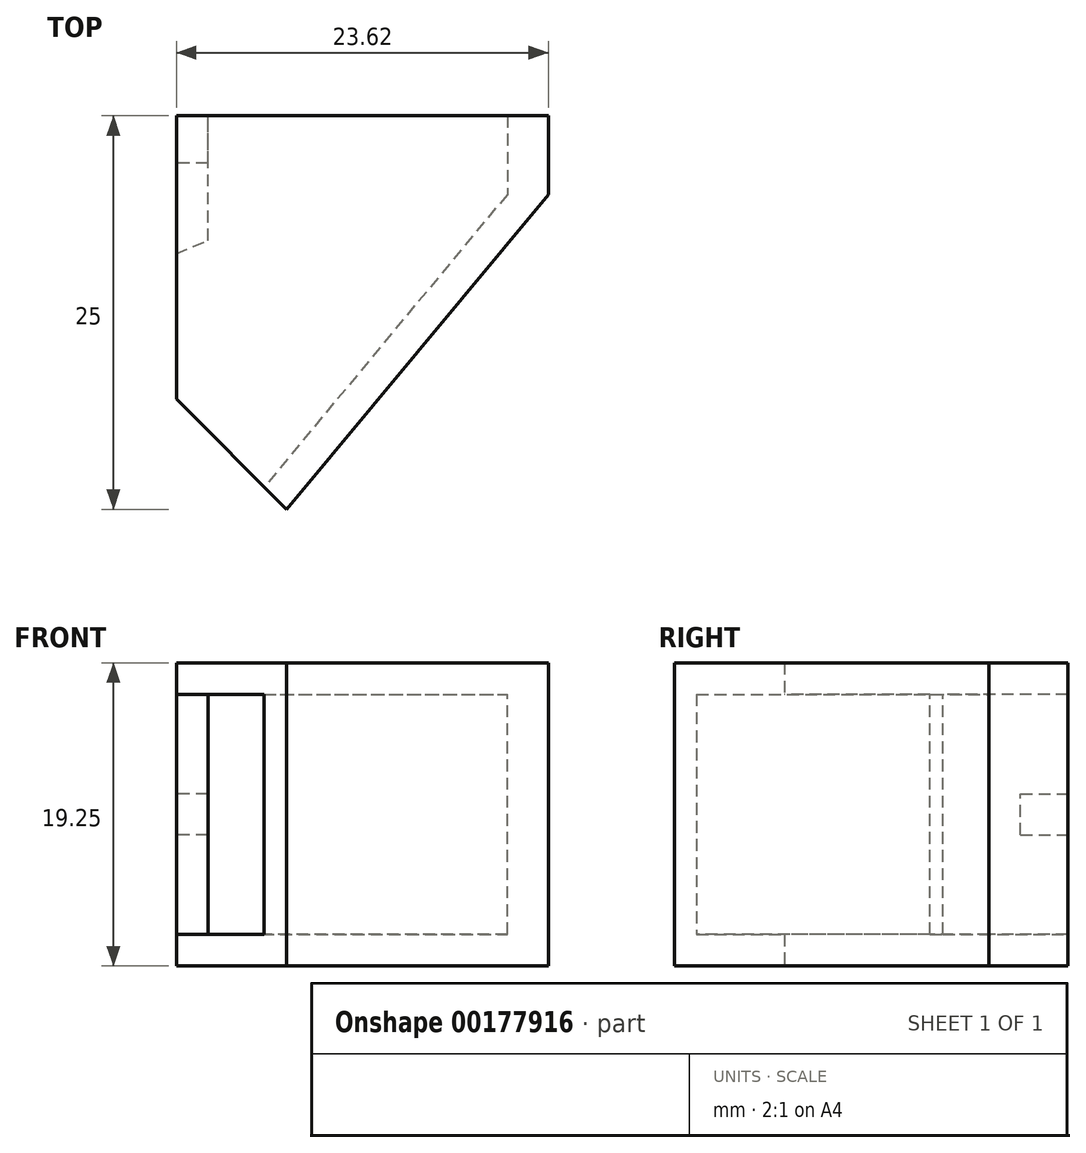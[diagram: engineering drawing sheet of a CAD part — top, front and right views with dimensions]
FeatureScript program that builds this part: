
annotation { "Feature Type Name" : "Feature", "Feature Type Description" : "" }
export const myFeature = defineFeature(function(context is Context, id is Id, definition is map)
    precondition{}
    {
        {
            var Q0;
            Q0=qCreatedBy(makeId("Front.planeOp"),FACE);
            var sketch = newSketch(context, id + "F0", { "sketchPlane" : qUnion([Q0])});
            skLineSegment(sketch, "E0.bottom", {"start": v(-2, -2) * mm, "end": v(21.62, -2) * mm});
            skLineSegment(sketch, "E0.top", {"start": v(-2, 17.25) * mm, "end": v(21.62, 17.25) * mm});
            skLineSegment(sketch, "E0.left", {"start": v(-2, -2) * mm, "end": v(-2, 17.25) * mm});
            skLineSegment(sketch, "E0.right", {"start": v(21.62, -2) * mm, "end": v(21.62, 17.25) * mm});
            skSolve(sketch);
        }
        {
            var Q0;
            Q0=qCreatedBy(makeId("Front.planeOp"),FACE);
            cPlane(context, id + "F1", {"entities" : qUnion([Q0]), "cplaneType" : CPlaneType.OFFSET, "offset" : 20 * mm, "width" : 150 * mm, "height" : 150 * mm});
        }
        {
            var Q0;
            Q0=qCreatedBy(id+"F1.planeOp",FACE);
            var sketch = newSketch(context, id + "F2", { "sketchPlane" : qUnion([Q0])});
            skLineSegment(sketch, "E1.bottom", {"start": v(-2, -2) * mm, "end": v(5, -2) * mm});
            skLineSegment(sketch, "E1.top", {"start": v(-2, 17.25) * mm, "end": v(5, 17.25) * mm});
            skLineSegment(sketch, "E1.left", {"start": v(-2, -2) * mm, "end": v(-2, 17.25) * mm});
            skLineSegment(sketch, "E1.right", {"start": v(5, -2) * mm, "end": v(5, 17.25) * mm});
            skSolve(sketch);
        }
        {
            var Q0;
            Q0=makeQuery(id+"F0.imprint","IMPRINT",FACE,{"disambiguationData":[TD([[makeQuery(id+"F0.imprint","IMPRINT",EDGE,{"derivedFrom":sQuery(id+"F0.wireOp",EDGE,"E0.bottom")}),1.0]])]});
            var Q1;
            Q1=makeQuery(id+"F2.imprint","IMPRINT",FACE,{"disambiguationData":[TD([[makeQuery(id+"F2.imprint","IMPRINT",EDGE,{"derivedFrom":sQuery(id+"F2.wireOp",EDGE,"E1.bottom")}),1.0]])]});
            loft(context, id + "F3", {"sheetProfilesArray" : [{ "sheetProfileEntities" : qUnion([Q0]) }, { "sheetProfileEntities" : qUnion([Q1]) }]});
        }
        {
            var Q0;
            Q0=makeQuery(id+"F3.opLoft","CAP_FACE",FACE,{"disambiguationData":[OSD([makeQuery(id+"F2.imprint","IMPRINT",FACE,{"disambiguationData":[TD([[makeQuery(id+"F2.imprint","IMPRINT",EDGE,{"derivedFrom":sQuery(id+"F2.wireOp",EDGE,"E1.bottom")}),1.0]])]})])],"isStart":true});
            var Q1;
            Q1=makeQuery(id+"F3.opLoft","CAP_FACE",FACE,{"disambiguationData":[OSD([makeQuery(id+"F0.imprint","IMPRINT",FACE,{"disambiguationData":[TD([[makeQuery(id+"F0.imprint","IMPRINT",EDGE,{"derivedFrom":sQuery(id+"F0.wireOp",EDGE,"E0.bottom")}),1.0]])]})])],"isStart":true});
            shell(context, id + "F4", {"entities" : qUnion([Q0, Q1]), "thickness" : 2 * mm});
        }
        {
            var Q0;
            Q0=makeQuery(id+"F3.opLoft","SWEPT_FACE",FACE,{"disambiguationData":[OSD([sQuery(id+"F0.wireOp",EDGE,"E0.bottom"),sQuery(id+"F0.wireOp",EDGE,"E0.left"),sQuery(id+"F0.wireOp",EDGE,"E0.right"),sQuery(id+"F2.wireOp",EDGE,"E1.bottom"),sQuery(id+"F2.wireOp",EDGE,"E1.left"),sQuery(id+"F2.wireOp",EDGE,"E1.right")])]});
            var sketch = newSketch(context, id + "F5", { "sketchPlane" : qUnion([Q0])});
            skLineSegment(sketch, "E2", {"start": v(5, 20) * mm, "end": v(-2, 13) * mm});
            skSolve(sketch);
        }
        {
            var Q0;
            {var subQ0=sQuery(id+"F5.wireOp",EDGE,"E2");Q0=makeQuery(id+"F5.imprint","IMPRINT",FACE,{"disambiguationData":[TD([[makeQuery(id+"F5.imprint","IMPRINT",EDGE,{"derivedFrom":subQ0}),-1.0]])]});}
            extrude(context, id + "F6", {"entities" : qUnion([Q0]), "operationType" : NewBodyOperationType.REMOVE, "oppositeDirection" : true, "depth" : 25 * mm});
        }
        {
            var Q0;
            Q0=makeQuery(id+"F6.boolean.opBoolean","INTERSECT",EDGE,{"derivedFrom":[makeQuery(id+"F4.opShell","OFFSET_FACE",FACE,{"disambiguationData":[OSD([sQuery(id+"F0.wireOp",EDGE,"E0.bottom"),sQuery(id+"F0.wireOp",EDGE,"E0.top"),sQuery(id+"F0.wireOp",EDGE,"E0.left"),sQuery(id+"F2.wireOp",EDGE,"E1.bottom"),sQuery(id+"F2.wireOp",EDGE,"E1.top"),sQuery(id+"F2.wireOp",EDGE,"E1.left")])]}),makeQuery(id+"F6.opExtrude","SWEPT_FACE",FACE,{"disambiguationData":[OSD([sQuery(id+"F5.wireOp",EDGE,"E2")])]})]});
            chamfer(context, id + "F7", {"entities" : qUnion([Q0]), "width" : 5 * mm, "tangentPropagation" : true});
        }
        {
            var Q0;
            Q0=makeQuery(id+"F3.opLoft","CAP_FACE",FACE,{"disambiguationData":[OSD([makeQuery(id+"F0.imprint","IMPRINT",FACE,{"disambiguationData":[TD([[makeQuery(id+"F0.imprint","IMPRINT",EDGE,{"derivedFrom":sQuery(id+"F0.wireOp",EDGE,"E0.bottom")}),1.0]])]})])],"isStart":true});
            extrude(context, id + "F8", {"entities" : qUnion([Q0]), "operationType" : NewBodyOperationType.ADD, "depth" : 5 * mm});
        }
        {
            var Q0;
            Q0=makeQuery(id+"F8.opExtrude","CAP_FACE",FACE,{"disambiguationData":[OSD([makeQuery(id+"F0.imprint","IMPRINT",FACE,{"disambiguationData":[TD([[makeQuery(id+"F0.imprint","IMPRINT",EDGE,{"derivedFrom":sQuery(id+"F0.wireOp",EDGE,"E0.bottom")}),1.0]])]})])],"isStart":false});
            var sketch = newSketch(context, id + "F9", { "sketchPlane" : qUnion([Q0])});
            skLineSegment(sketch, "E3", {"start": v(0, 0) * mm, "end": v(0, 15.25) * mm});
            skLineSegment(sketch, "E4", {"start": v(0, 7.62) * mm, "end": v(2, 7.62) * mm});
            skLineSegment(sketch, "E5.top", {"start": v(0, 8.92) * mm, "end": v(2, 8.92) * mm});
            skLineSegment(sketch, "E5.left", {"start": v(0, 7.62) * mm, "end": v(0, 8.92) * mm});
            skLineSegment(sketch, "E5.right", {"start": v(2, 7.62) * mm, "end": v(2, 8.92) * mm});
            skLineSegment(sketch, "E6.top", {"start": v(0, 6.32) * mm, "end": v(2, 6.32) * mm});
            skLineSegment(sketch, "E6.left", {"start": v(0, 7.62) * mm, "end": v(0, 6.32) * mm});
            skLineSegment(sketch, "E6.right", {"start": v(2, 7.62) * mm, "end": v(2, 6.32) * mm});
            skSolve(sketch);
        }
        {
            var Q0;
            Q0=makeQuery(id+"F9.imprint","IMPRINT",FACE,{"disambiguationData":[TD([[makeQuery(id+"F9.imprint","IMPRINT",EDGE,{"derivedFrom":sQuery(id+"F9.wireOp",EDGE,"E4")}),-1.0]])]});
            var Q1;
            Q1=makeQuery(id+"F9.imprint","IMPRINT",FACE,{"disambiguationData":[TD([[makeQuery(id+"F9.imprint","IMPRINT",EDGE,{"derivedFrom":sQuery(id+"F9.wireOp",EDGE,"E5.top")}),-1.0]])]});
            extrude(context, id + "F10", {"entities" : qUnion([Q0, Q1]), "operationType" : NewBodyOperationType.REMOVE, "oppositeDirection" : true, "depth" : 3 * mm});
        }
    });
